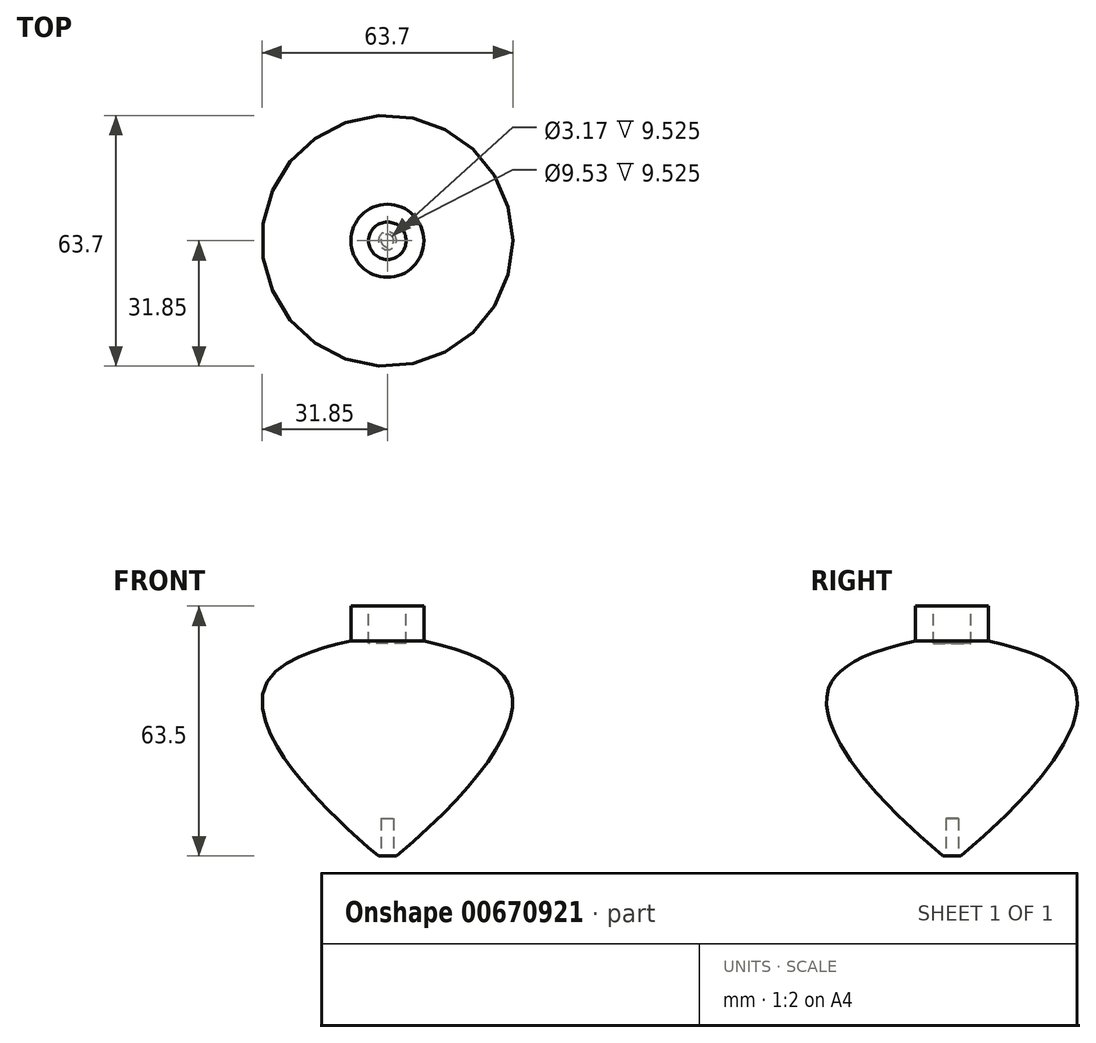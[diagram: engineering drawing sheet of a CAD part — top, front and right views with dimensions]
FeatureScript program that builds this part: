
annotation { "Feature Type Name" : "Feature", "Feature Type Description" : "" }
export const myFeature = defineFeature(function(context is Context, id is Id, definition is map)
    precondition{}
    {
        {
            var Q0;
            Q0=qCreatedBy(makeId("Front.planeOp"),FACE);
            var sketch = newSketch(context, id + "F0", { "sketchPlane" : qUnion([Q0])});
            skLineSegment(sketch, "E0", {"start": v(9.27, 14) * mm, "end": v(9.27, 22.78) * mm});
            skLineSegment(sketch, "E1", {"start": v(9.27, 22.78) * mm, "end": v(0, 22.78) * mm});
            skLineSegment(sketch, "E2", {"start": v(0, 22.78) * mm, "end": v(0, -40.72) * mm});
            skFitSpline(sketch, "E3", {"points": [v(2.28, -40.72) * mm, v(31.75, 0) * mm, v(9.27, 14) * mm], "startDerivative": vector(100.17, 84.5) * mm, "endDerivative": vector(-99.3, 22.46) * mm});
            skLineSegment(sketch, "E4", {"start": v(0, -40.72) * mm, "end": v(2.28, -40.72) * mm});
            skSolve(sketch);
        }
        {
            var Q0;
            Q0 = qSketchRegion(id + "F0", true);
            var Q1;
            Q1=sQuery(id+"F0.wireOp",EDGE,"E2");
            revolve(context, id + "F1", {"entities" : qUnion([Q0]), "axis" : qUnion([Q1]), "revolveType" : RevolveType.FULL});
        }
        {
            var Q0;
            Q0=makeQuery(id+"F1.opRevolve","SWEPT_FACE",FACE,{"disambiguationData":[OSD([sQuery(id+"F0.wireOp",EDGE,"E4")])]});
            var sketch = newSketch(context, id + "F2", { "sketchPlane" : qUnion([Q0])});
            skCircle(sketch, "E5", {"center": v(0, 0) * mm, "radius": 1.59 * mm});
            skSolve(sketch);
        }
        {
            var Q0;
            Q0 = qSketchRegion(id + "F2", true);
            extrude(context, id + "F3", {"entities" : qUnion([Q0]), "operationType" : NewBodyOperationType.REMOVE, "oppositeDirection" : true, "depth" : 9.52 * mm, "offsetDistance" : 25.4 * mm});
        }
        {
            var Q0;
            Q0=makeQuery(id+"F1.opRevolve","SWEPT_FACE",FACE,{"disambiguationData":[OSD([sQuery(id+"F0.wireOp",EDGE,"E1")])]});
            var sketch = newSketch(context, id + "F4", { "sketchPlane" : qUnion([Q0])});
            skCircle(sketch, "E6", {"center": v(0, 0) * mm, "radius": 4.76 * mm});
            skSolve(sketch);
        }
        {
            var Q0;
            Q0 = qSketchRegion(id + "F4", true);
            extrude(context, id + "F5", {"entities" : qUnion([Q0]), "operationType" : NewBodyOperationType.REMOVE, "oppositeDirection" : true, "depth" : 9.52 * mm, "offsetDistance" : 25.4 * mm});
        }
    });
